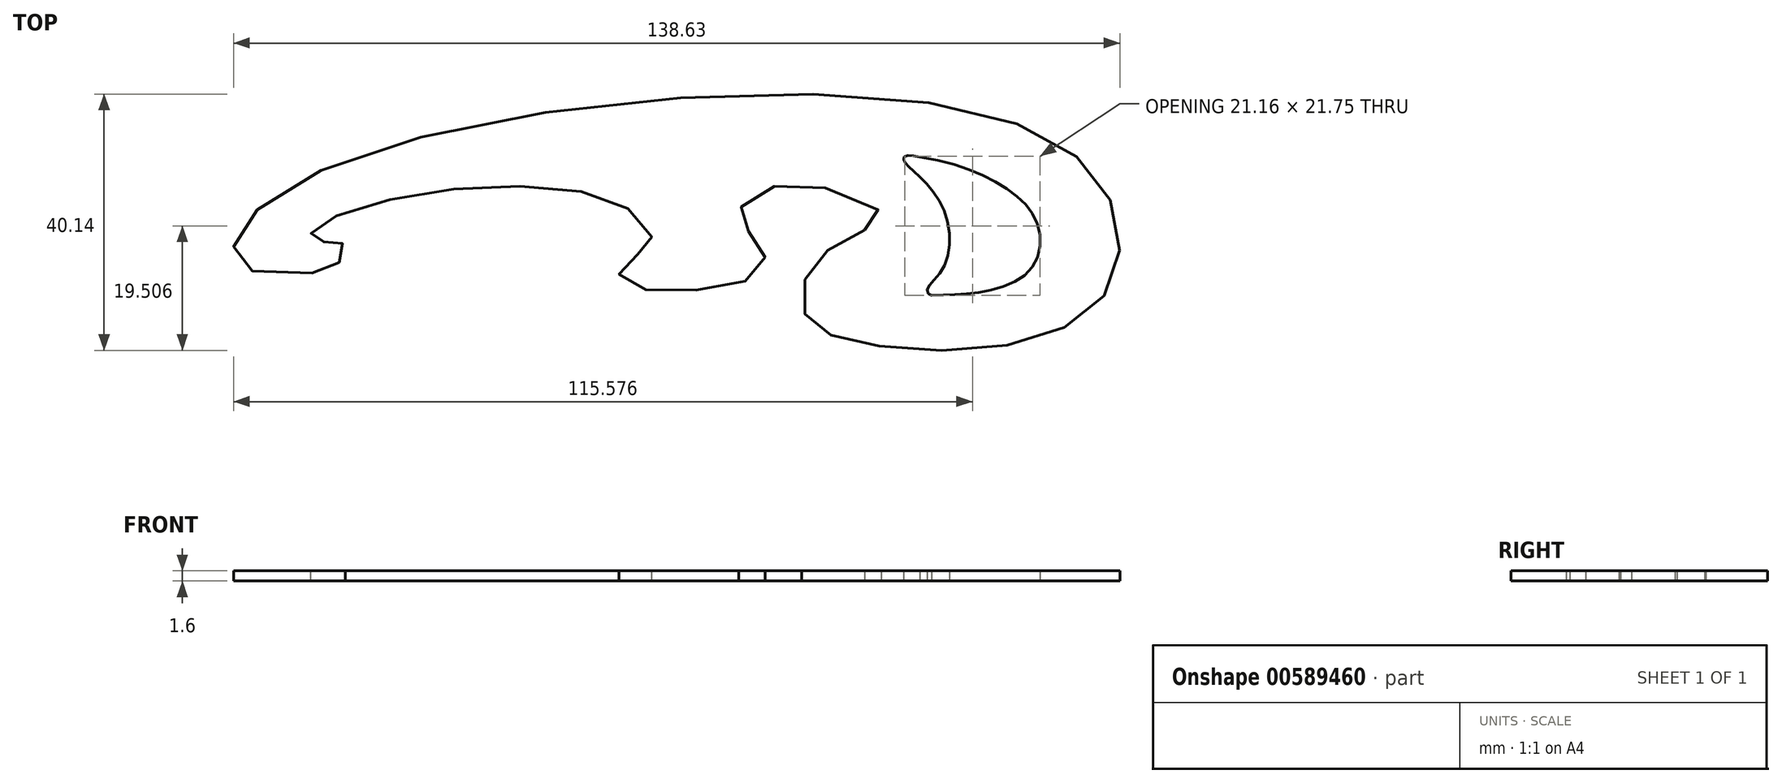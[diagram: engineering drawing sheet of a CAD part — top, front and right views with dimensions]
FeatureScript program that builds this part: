
annotation { "Feature Type Name" : "Feature", "Feature Type Description" : "" }
export const myFeature = defineFeature(function(context is Context, id is Id, definition is map)
    precondition{}
    {
        {
            var Q0;
            Q0=qCreatedBy(makeId("Top.planeOp"),FACE);
            var sketch = newSketch(context, id + "F0", { "sketchPlane" : qUnion([Q0])});
            skFitSpline(sketch, "E0", {"points": [v(-59.43, -11.75) * mm, v(-71.63, -8.56) * mm, v(-57.33, 4.6) * mm, v(37.4, 14.89) * mm, v(64.88, 0.76) * mm, v(65.2, -14.17) * mm, v(49.57, -23.02) * mm, v(25.23, -22.47) * mm, v(17.76, -18.32) * mm, v(18.59, -10.85) * mm, v(27.02, -5.04) * mm], "startDerivative": vector(-285.76, -42.7) * mm, "endDerivative": vector(144.61, 67.97) * mm});
            skFitSpline(sketch, "E1", {"points": [v(27.02, -5.04) * mm, v(29.7, -2.9) * mm, v(21.61, 1.4) * mm, v(11.93, 1.54) * mm, v(7.6, -1.64) * mm, v(7.89, -4.31) * mm, v(10.49, -6.7) * mm, v(11.36, -10.16) * mm, v(8.47, -12.98) * mm, v(-1.07, -14.5) * mm, v(-9.3, -13.92) * mm, v(-11.4, -11.9) * mm, v(-9.37, -9.15) * mm, v(-7.71, -8.57) * mm, v(-6.27, -6.7) * mm, v(-8.3, -2.94) * mm, v(-15.66, 0.67) * mm, v(-29.96, 1.83) * mm, v(-46.14, 0) * mm, v(-56.83, -3.37) * mm, v(-59.43, -5.3) * mm, v(-59.5, -6.4) * mm, v(-58.6, -6.86) * mm, v(-56.4, -6.79) * mm, v(-55.23, -6.71) * mm, v(-54.35, -7.64) * mm, v(-54.44, -9.3) * mm, v(-56.08, -10.62) * mm, v(-59.43, -11.75) * mm], "startDerivative": vector(84.81, 42.78) * mm, "endDerivative": vector(-100.79, -14.2) * mm});
            skFitSpline(sketch, "E2", {"points": [v(35.64, 6.4) * mm, v(48.9, 1.69) * mm, v(54.07, -4.19) * mm, v(53.08, -11.05) * mm, v(45.64, -14.66) * mm, v(37.5, -15.24) * mm], "startDerivative": vector(66.6, -9.71) * mm, "endDerivative": vector(-41.63, -0.44) * mm});
            skFitSpline(sketch, "E3", {"points": [v(37.5, -15.24) * mm, v(36.78, -14.46) * mm, v(39.11, -11.3) * mm, v(39.51, -2.09) * mm, v(34.69, 4.19) * mm, v(33.14, 5.92) * mm, v(33.37, 6.55) * mm, v(35.64, 6.4) * mm], "startDerivative": vector(-12.18, 0) * mm, "endDerivative": vector(22.6, -3.75) * mm});
            skSolve(sketch);
        }
        {
            var Q0;
            Q0 = qSketchRegion(id + "F0", true);
            extrude(context, id + "F1", {"entities" : qUnion([Q0]), "depth" : 1.6 * mm, "offsetDistance" : 25.4 * mm});
        }
    });
